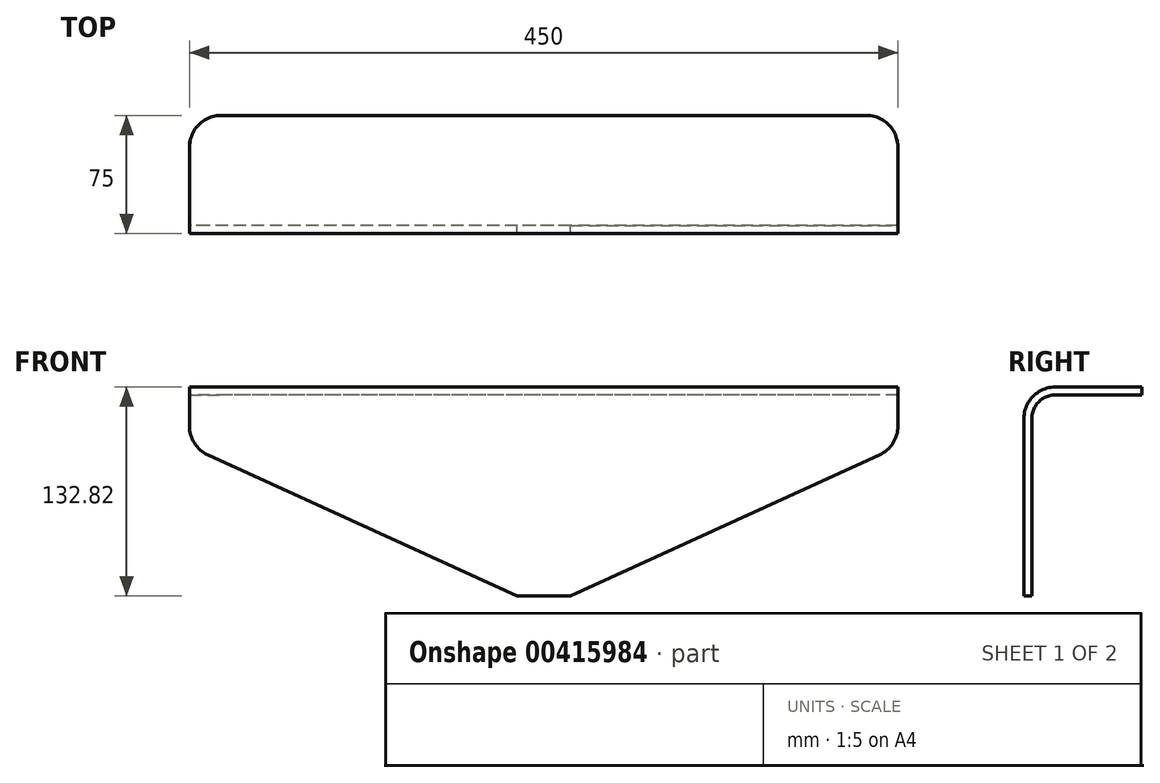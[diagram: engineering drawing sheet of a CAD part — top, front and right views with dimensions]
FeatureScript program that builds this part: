
annotation { "Feature Type Name" : "Feature", "Feature Type Description" : "" }
export const myFeature = defineFeature(function(context is Context, id is Id, definition is map)
    precondition{}
    {
        {
            var Q0;
            Q0=qCreatedBy(makeId("Front.planeOp"),FACE);
            var sketch = newSketch(context, id + "F0", { "sketchPlane" : qUnion([Q0])});
            skLineSegment(sketch, "E0.left", {"start": v(224.92, 175.06) * mm, "end": v(225, 150.06) * mm});
            skPoint(sketch, "E0.middle", {"position": v(0, 0) * mm});
            skLineSegment(sketch, "E1.0", {"start": v(61.68, 62.5) * mm, "end": v(61.68, 62.5) * mm});
            skLineSegment(sketch, "E2", {"start": v(61.68, 62.5) * mm, "end": v(213.32, 131.81) * mm});
            skPoint(sketch, "E3.orphan", {"position": v(-224.92, -175.06) * mm});
            skPoint(sketch, "E4.orphan", {"position": v(226.2, -232.01) * mm});
            skPoint(sketch, "E5.visualSharp", {"position": v(-225, 137.15) * mm});
            skPoint(sketch, "E6.visualSharp", {"position": v(225.04, 137.17) * mm});
            skArc(sketch, "E6.filletArc", {"start": v(213.32, 131.81) * mm, "mid": v(221.84, 139.22) * mm, "end": v(225, 150.06) * mm});
            skLineSegment(sketch, "E7", {"start": v(225, 150.06) * mm, "end": v(205, 150) * mm});
            skPoint(sketch, "E8.0.start.orphan", {"position": v(-29.55, -156.81) * mm});
            skPoint(sketch, "E0.right.start.orphan", {"position": v(-226.2, 232.01) * mm});
            skPoint(sketch, "E9.visualSharp", {"position": v(61.68, 62.5) * mm});
            skLineSegment(sketch, "E10", {"start": v(291.15, 62.5) * mm, "end": v(291.15, 178.07) * mm});
            skLineSegment(sketch, "E11", {"start": v(291.15, 178.07) * mm, "end": v(224.92, 175.06) * mm});
            skPoint(sketch, "E12.start.orphan", {"position": v(-0.64, 203.54) * mm});
            skPoint(sketch, "E0.top.end.orphan", {"position": v(16.07, -47.16) * mm});
            skLineSegment(sketch, "E13", {"start": v(213.32, 131.81) * mm, "end": v(-75.02, 0) * mm});
            skLineSegment(sketch, "E14", {"start": v(-75.02, 0) * mm, "end": v(292.98, 0) * mm});
            skLineSegment(sketch, "E15", {"start": v(292.98, 0) * mm, "end": v(291.15, 62.5) * mm});
            skSolve(sketch);
        }
        {
            var Q0;
            Q0=qCreatedBy(makeId("Right.planeOp"),FACE);
            var sketch = newSketch(context, id + "F1", { "sketchPlane" : qUnion([Q0])});
            skLineSegment(sketch, "E16", {"start": v(0, 42.04) * mm, "end": v(0, 154.86) * mm});
            skLineSegment(sketch, "E17", {"start": v(20, 174.86) * mm, "end": v(75, 174.86) * mm});
            skPoint(sketch, "E18.visualSharp", {"position": v(0, 174.86) * mm});
            skArc(sketch, "E18.filletArc", {"start": v(20, 174.86) * mm, "mid": v(5.86, 169) * mm, "end": v(0, 154.86) * mm});
            skLineSegment(sketch, "E19.0", {"start": v(20, 169.86) * mm, "end": v(75, 169.86) * mm});
            skArc(sketch, "E20.0", {"start": v(20, 169.86) * mm, "mid": v(9.4, 165.46) * mm, "end": v(5, 154.86) * mm});
            skLineSegment(sketch, "E21.0", {"start": v(5, 42.04) * mm, "end": v(5, 154.86) * mm});
            skLineSegment(sketch, "E22", {"start": v(75, 174.86) * mm, "end": v(75, 169.86) * mm});
            skLineSegment(sketch, "E23", {"start": v(0, 42.04) * mm, "end": v(5, 42.04) * mm});
            skSolve(sketch);
        }
        {
            var Q0;
            Q0 = qSketchRegion(id + "F1", true);
            extrude(context, id + "F2", {"entities" : qUnion([Q0]), "depth" : 250 * mm});
        }
        {
            var Q0;
            Q0 = qSketchRegion(id + "F0", true);
            extrude(context, id + "F3", {"entities" : qUnion([Q0]), "operationType" : NewBodyOperationType.REMOVE, "oppositeDirection" : true, "depth" : 100 * mm});
        }
        {
            var Q0;
            Q0=makeQuery(id+"F3.boolean.opBoolean","INTERSECT",EDGE,{"derivedFrom":[makeQuery(id+"F2.opExtrude","SWEPT_FACE",FACE,{"disambiguationData":[OSD([sQuery(id+"F1.wireOp",EDGE,"E22")])]}),makeQuery(id+"F3.opExtrude","SWEPT_FACE",FACE,{"disambiguationData":[OSD([sQuery(id+"F0.wireOp",EDGE,"E0.left")])]})]});
            fillet(context, id + "F4", {"entities" : qUnion([Q0]), "radius" : 20 * mm, "tangentPropagation" : true, "allowEdgeOverflow" : false});
        }
        {
            var Q0;
            Q0=makeQuery(id+"F2.opExtrude","SWEPT_BODY",BODY,{"disambiguationData":[OSD([sQuery(id+"F1.wireOp",EDGE,"E16"),sQuery(id+"F1.wireOp",EDGE,"E17"),sQuery(id+"F1.wireOp",EDGE,"E18.filletArc"),sQuery(id+"F1.wireOp",EDGE,"E19.0"),sQuery(id+"F1.wireOp",EDGE,"E20.0"),sQuery(id+"F1.wireOp",EDGE,"E21.0"),sQuery(id+"F1.wireOp",EDGE,"E22"),sQuery(id+"F1.wireOp",EDGE,"E23")])]});
            var Q1;
            Q1=qCreatedBy(makeId("Right.planeOp"),FACE);
            mirror(context, id + "F5", {"operationType" : NewBodyOperationType.ADD, "entities" : qUnion([Q0]), "mirrorPlane" : qUnion([Q1])});
        }
    });
